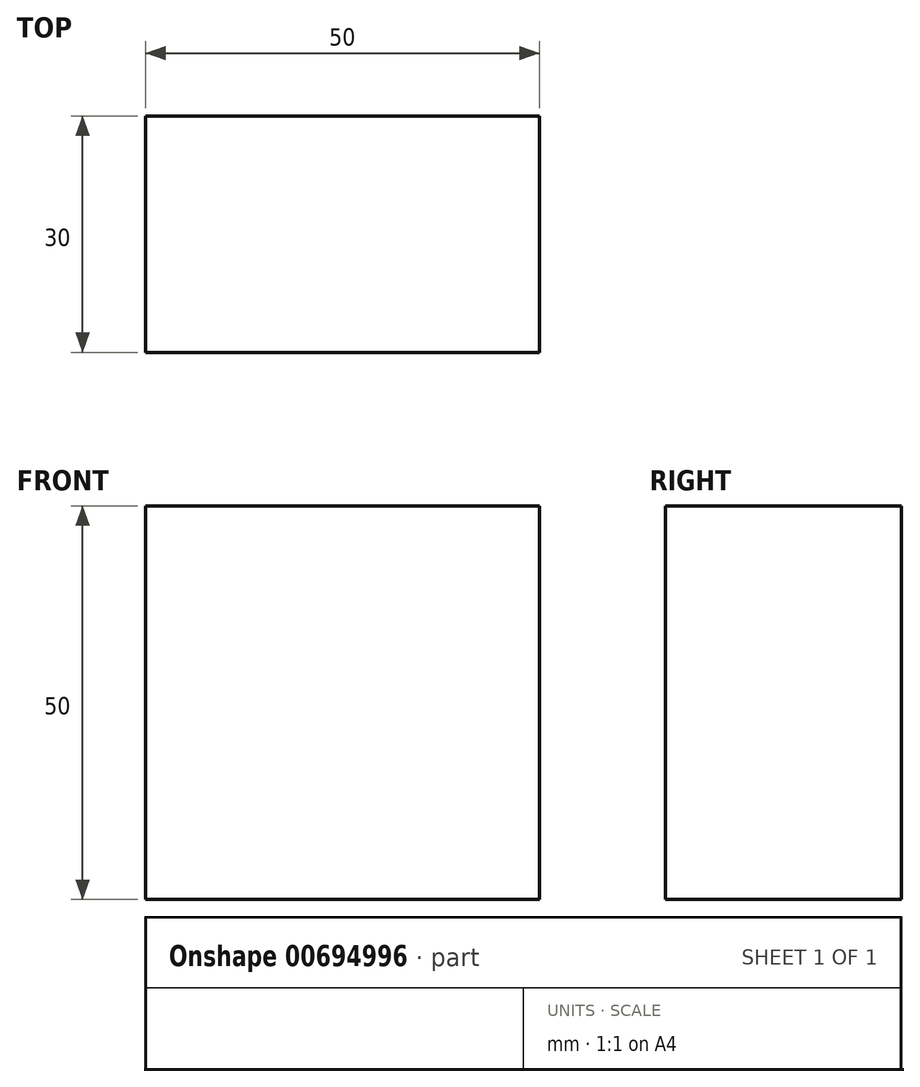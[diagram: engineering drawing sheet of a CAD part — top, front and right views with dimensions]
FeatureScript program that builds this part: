
annotation { "Feature Type Name" : "Feature", "Feature Type Description" : "" }
export const myFeature = defineFeature(function(context is Context, id is Id, definition is map)
    precondition{}
    {
        {
            var Q0;
            Q0=qCreatedBy(makeId("Front.planeOp"),FACE);
            var sketch = newSketch(context, id + "F0", { "sketchPlane" : qUnion([Q0])});
            skLineSegment(sketch, "E0", {"start": v(0, 0) * mm, "end": v(0, 30) * mm});
            skLineSegment(sketch, "E1", {"start": v(0, 0) * mm, "end": v(30, 0) * mm});
            skLineSegment(sketch, "E2", {"start": v(0, 30) * mm, "end": v(30, 0) * mm});
            skSolve(sketch);
        }
        {
            var Q0;
            Q0 = qSketchRegion(id + "F0", true);
            extrude(context, id + "F1", {"entities" : qUnion([Q0]), "depth" : 15 * mm, "offsetDistance" : 25 * mm});
        }
        {
            var Q0;
            Q0=qCreatedBy(makeId("Front.planeOp"),FACE);
            cPlane(context, id + "F2", {"entities" : qUnion([Q0]), "cplaneType" : CPlaneType.OFFSET, "offset" : 15 * mm, "oppositeDirection" : true, "width" : 150 * mm, "height" : 150 * mm});
        }
        {
            var Q0;
            Q0=qCreatedBy(id+"F2.planeOp",FACE);
            var sketch = newSketch(context, id + "F3", { "sketchPlane" : qUnion([Q0])});
            skLineSegment(sketch, "E3.bottom", {"start": v(0, 0) * mm, "end": v(50, 0) * mm});
            skLineSegment(sketch, "E3.top", {"start": v(0, 50) * mm, "end": v(50, 50) * mm});
            skLineSegment(sketch, "E3.left", {"start": v(0, 0) * mm, "end": v(0, 50) * mm});
            skLineSegment(sketch, "E3.right", {"start": v(50, 0) * mm, "end": v(50, 50) * mm});
            skSolve(sketch);
        }
        {
            var Q0;
            Q0=makeQuery(id+"F3.imprint","IMPRINT",FACE,{"disambiguationData":[TD([[makeQuery(id+"F3.imprint","IMPRINT",EDGE,{"derivedFrom":sQuery(id+"F3.wireOp",EDGE,"E3.bottom")}),1.0]])]});
            extrude(context, id + "F4", {"entities" : qUnion([Q0]), "operationType" : NewBodyOperationType.ADD, "depth" : 30 * mm, "offsetDistance" : 25 * mm});
        }
    });
